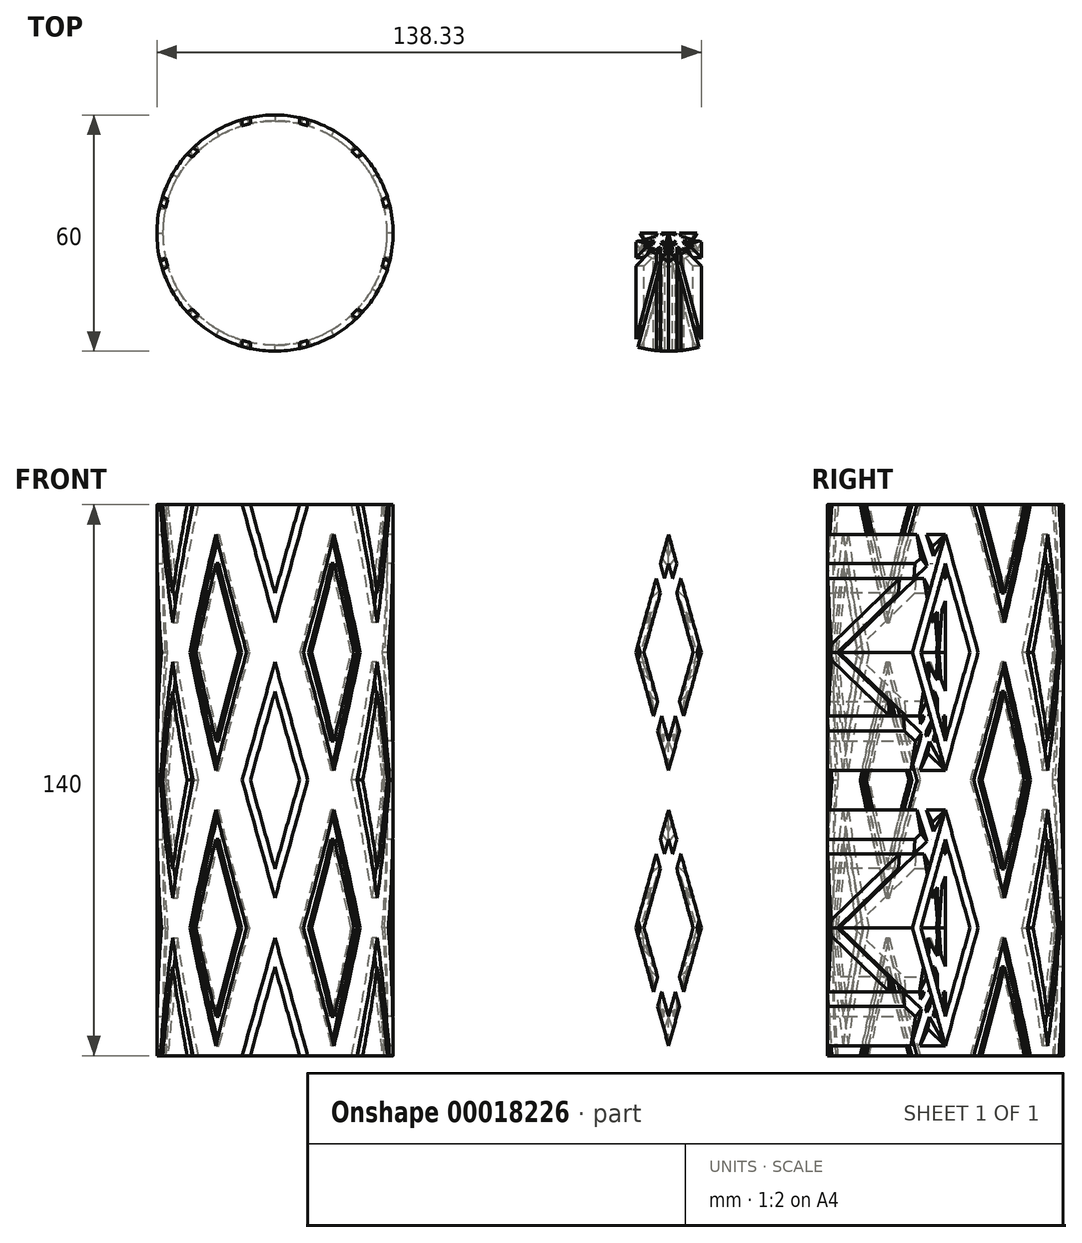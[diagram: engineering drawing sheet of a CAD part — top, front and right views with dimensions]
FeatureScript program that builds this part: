
annotation { "Feature Type Name" : "Feature", "Feature Type Description" : "" }
export const myFeature = defineFeature(function(context is Context, id is Id, definition is map)
    precondition{}
    {
        {
            var Q0;
            Q0=qCreatedBy(makeId("Top.planeOp"),FACE);
            var sketch = newSketch(context, id + "F0", { "sketchPlane" : qUnion([Q0])});
            skCircle(sketch, "E0", {"center": v(0, 0) * mm, "radius": 30 * mm});
            skCircle(sketch, "E1", {"center": v(0, 0) * mm, "radius": 28.5 * mm});
            skSolve(sketch);
        }
        {
            var Q0;
            Q0=makeQuery(id+"F0.imprint","IMPRINT",FACE,{"disambiguationData":[TD([[makeQuery(id+"F0.imprint","IMPRINT",EDGE,{"derivedFrom":sQuery(id+"F0.wireOp",EDGE,"E0")}),1.0]])]});
            extrude(context, id + "F1", {"entities" : qUnion([Q0]), "depth" : 140 * mm});
        }
        {
            var Q0;
            Q0=qCreatedBy(makeId("Front.planeOp"),FACE);
            var sketch = newSketch(context, id + "F2", { "sketchPlane" : qUnion([Q0])});
            skLineSegment(sketch, "E2", {"start": v(-6.25, 0) * mm, "end": v(0, 22.5) * mm});
            skLineSegment(sketch, "E3", {"start": v(0, 22.5) * mm, "end": v(6.25, 0) * mm});
            skLineSegment(sketch, "E4", {"start": v(-6.25, 0) * mm, "end": v(0, -22.5) * mm});
            skLineSegment(sketch, "E5", {"start": v(0, -22.5) * mm, "end": v(6.25, 0) * mm});
            skLineSegment(sketch, "E6", {"start": v(0, 47.5) * mm, "end": v(-6.25, 70) * mm});
            skLineSegment(sketch, "E7", {"start": v(-6.25, 70) * mm, "end": v(0, 92.5) * mm});
            skLineSegment(sketch, "E8", {"start": v(0, 92.5) * mm, "end": v(6.25, 70) * mm});
            skLineSegment(sketch, "E9", {"start": v(6.25, 70) * mm, "end": v(0, 47.5) * mm});
            skLineSegment(sketch, "E10", {"start": v(0, 117.5) * mm, "end": v(-6.25, 140) * mm});
            skLineSegment(sketch, "E11", {"start": v(-6.25, 140) * mm, "end": v(0, 162.5) * mm});
            skLineSegment(sketch, "E12", {"start": v(0, 162.5) * mm, "end": v(6.25, 140) * mm});
            skLineSegment(sketch, "E13", {"start": v(6.25, 140) * mm, "end": v(0, 117.5) * mm});
            skLineSegment(sketch, "E14", {"start": v(0, 140) * mm, "end": v(0, 0) * mm, "construction": true});
            skPoint(sketch, "E15", {"position": v(0, 70) * mm});
            skLineSegment(sketch, "E16", {"start": v(-6.25, 70) * mm, "end": v(6.25, 70) * mm, "construction": true});
            skLineSegment(sketch, "E17.0", {"start": v(-8.33, 140) * mm, "end": v(0, 169.97) * mm});
            skLineSegment(sketch, "E17.1", {"start": v(0, 110.03) * mm, "end": v(-8.33, 140) * mm});
            skLineSegment(sketch, "E17.2", {"start": v(8.33, 140) * mm, "end": v(0, 110.03) * mm});
            skLineSegment(sketch, "E17.3", {"start": v(0, 169.97) * mm, "end": v(8.33, 140) * mm});
            skLineSegment(sketch, "E18.0", {"start": v(0, 99.97) * mm, "end": v(8.33, 70) * mm});
            skLineSegment(sketch, "E18.1", {"start": v(-8.33, 70) * mm, "end": v(0, 99.97) * mm});
            skLineSegment(sketch, "E18.2", {"start": v(0, 40.03) * mm, "end": v(-8.33, 70) * mm});
            skLineSegment(sketch, "E18.3", {"start": v(8.33, 70) * mm, "end": v(0, 40.03) * mm});
            skLineSegment(sketch, "E19.0", {"start": v(0, 29.97) * mm, "end": v(8.33, 0) * mm});
            skLineSegment(sketch, "E19.1", {"start": v(-8.33, 0) * mm, "end": v(0, 29.97) * mm});
            skLineSegment(sketch, "E19.2", {"start": v(-8.33, 0) * mm, "end": v(0, -29.97) * mm});
            skLineSegment(sketch, "E19.3", {"start": v(0, -29.97) * mm, "end": v(8.33, 0) * mm});
            skSolve(sketch);
        }
        {
            var Q0;
            Q0=makeQuery(id+"F2.imprint","IMPRINT",FACE,{"disambiguationData":[TD([[makeQuery(id+"F2.imprint","IMPRINT",EDGE,{"derivedFrom":sQuery(id+"F2.wireOp",EDGE,"E10")}),1.0]])]});
            var Q1;
            Q1=makeQuery(id+"F2.imprint","IMPRINT",FACE,{"disambiguationData":[TD([[makeQuery(id+"F2.imprint","IMPRINT",EDGE,{"derivedFrom":sQuery(id+"F2.wireOp",EDGE,"E6")}),1.0]])]});
            var Q2;
            Q2=makeQuery(id+"F2.imprint","IMPRINT",FACE,{"disambiguationData":[TD([[makeQuery(id+"F2.imprint","IMPRINT",EDGE,{"derivedFrom":sQuery(id+"F2.wireOp",EDGE,"E2")}),1.0]])]});
            var Q3;
            Q3=makeQuery(id+"F1.opExtrude","SWEPT_FACE",FACE,{"disambiguationData":[OSD([sQuery(id+"F0.wireOp",EDGE,"E0")])]});
            extrude(context, id + "F3", {"entities" : qUnion([Q0, Q1, Q2]), "endBound" : BoundingType.UP_TO_SURFACE, "endBoundEntityFace" : qUnion([Q3]), "depth" : 25 * mm});
        }
        {
            var Q0;
            Q0=makeQuery(id+"F3.opExtrude","SWEPT_BODY",BODY,{"disambiguationData":[OSD([sQuery(id+"F2.wireOp",EDGE,"E6"),sQuery(id+"F2.wireOp",EDGE,"E7"),sQuery(id+"F2.wireOp",EDGE,"E8"),sQuery(id+"F2.wireOp",EDGE,"E9"),sQuery(id+"F2.wireOp",EDGE,"E18.0"),sQuery(id+"F2.wireOp",EDGE,"E18.1"),sQuery(id+"F2.wireOp",EDGE,"E18.2"),sQuery(id+"F2.wireOp",EDGE,"E18.3")])]});
            var Q1;
            Q1=makeQuery(id+"F3.opExtrude","SWEPT_BODY",BODY,{"disambiguationData":[OSD([sQuery(id+"F2.wireOp",EDGE,"E2"),sQuery(id+"F2.wireOp",EDGE,"E3"),sQuery(id+"F2.wireOp",EDGE,"E4"),sQuery(id+"F2.wireOp",EDGE,"E5"),sQuery(id+"F2.wireOp",EDGE,"E19.0"),sQuery(id+"F2.wireOp",EDGE,"E19.1"),sQuery(id+"F2.wireOp",EDGE,"E19.2"),sQuery(id+"F2.wireOp",EDGE,"E19.3")])]});
            var Q2;
            Q2=sQuery(id+"F2.wireOp",EDGE,"E14");
            transform(context, id + "F4", {"entities" : qUnion([Q0, Q1]), "transformType" : TransformType.TRANSLATION_DISTANCE, "transformDirection" : qUnion([Q2]), "distance" : 32.5 * mm, "oppositeDirection" : true, "makeCopy" : true});
        }
        {
            var Q0;
            Q0=makeQuery(id+"F4.opPattern","COPY",BODY,{"derivedFrom":makeQuery(id+"F3.opExtrude","SWEPT_BODY",BODY,{"disambiguationData":[OSD([sQuery(id+"F2.wireOp",EDGE,"E6"),sQuery(id+"F2.wireOp",EDGE,"E7"),sQuery(id+"F2.wireOp",EDGE,"E8"),sQuery(id+"F2.wireOp",EDGE,"E9"),sQuery(id+"F2.wireOp",EDGE,"E18.0"),sQuery(id+"F2.wireOp",EDGE,"E18.1"),sQuery(id+"F2.wireOp",EDGE,"E18.2"),sQuery(id+"F2.wireOp",EDGE,"E18.3")])]}),"instanceName":"1"});
            var Q1;
            Q1=makeQuery(id+"F4.opPattern","COPY",BODY,{"derivedFrom":makeQuery(id+"F3.opExtrude","SWEPT_BODY",BODY,{"disambiguationData":[OSD([sQuery(id+"F2.wireOp",EDGE,"E2"),sQuery(id+"F2.wireOp",EDGE,"E3"),sQuery(id+"F2.wireOp",EDGE,"E4"),sQuery(id+"F2.wireOp",EDGE,"E5"),sQuery(id+"F2.wireOp",EDGE,"E19.0"),sQuery(id+"F2.wireOp",EDGE,"E19.1"),sQuery(id+"F2.wireOp",EDGE,"E19.2"),sQuery(id+"F2.wireOp",EDGE,"E19.3")])]}),"instanceName":"1"});
            var Q2;
            {var subQ0=sQuery(id+"F0.wireOp",EDGE,"E0");Q2=makeQuery(id+"F7.boolean.opBoolean","SPLIT",EDGE,{"disambiguationData":[TD([makeQuery(id+"F3.opExtrude","SWEPT_FACE",FACE,{"disambiguationData":[OSD([sQuery(id+"F2.wireOp",EDGE,"E17.2")])]})])],"derivedFrom":makeQuery(id+"F1.opExtrude","CAP_EDGE",EDGE,{"disambiguationData":[OSD([subQ0])],"isStart":false})});}
            circularPattern(context, id + "F5", {"entities" : qUnion([Q0, Q1]), "axis" : qUnion([Q2]), "angle" : 30 * degree, "instanceCount" : 2});
        }
        {
            var Q0;
            Q0=makeQuery(id+"F5.opPattern","COPY",BODY,{"derivedFrom":makeQuery(id+"F4.opPattern","COPY",BODY,{"derivedFrom":makeQuery(id+"F3.opExtrude","SWEPT_BODY",BODY,{"disambiguationData":[OSD([sQuery(id+"F2.wireOp",EDGE,"E6"),sQuery(id+"F2.wireOp",EDGE,"E7"),sQuery(id+"F2.wireOp",EDGE,"E8"),sQuery(id+"F2.wireOp",EDGE,"E9"),sQuery(id+"F2.wireOp",EDGE,"E18.0"),sQuery(id+"F2.wireOp",EDGE,"E18.1"),sQuery(id+"F2.wireOp",EDGE,"E18.2"),sQuery(id+"F2.wireOp",EDGE,"E18.3")])]}),"instanceName":"1"}),"instanceName":"1"});
            var Q1;
            Q1=makeQuery(id+"F5.opPattern","COPY",BODY,{"derivedFrom":makeQuery(id+"F4.opPattern","COPY",BODY,{"derivedFrom":makeQuery(id+"F3.opExtrude","SWEPT_BODY",BODY,{"disambiguationData":[OSD([sQuery(id+"F2.wireOp",EDGE,"E2"),sQuery(id+"F2.wireOp",EDGE,"E3"),sQuery(id+"F2.wireOp",EDGE,"E4"),sQuery(id+"F2.wireOp",EDGE,"E5"),sQuery(id+"F2.wireOp",EDGE,"E19.0"),sQuery(id+"F2.wireOp",EDGE,"E19.1"),sQuery(id+"F2.wireOp",EDGE,"E19.2"),sQuery(id+"F2.wireOp",EDGE,"E19.3")])]}),"instanceName":"1"}),"instanceName":"1"});
            var Q2;
            Q2=makeQuery(id+"F1.opExtrude","CAP_EDGE",EDGE,{"disambiguationData":[OSD([sQuery(id+"F0.wireOp",EDGE,"E0")])],"isStart":false});
            circularPattern(context, id + "F6", {"operationType" : NewBodyOperationType.REMOVE, "entities" : qUnion([Q0, Q1]), "axis" : qUnion([Q2]), "angle" : 360 * degree, "instanceCount" : 6, "equalSpace" : true});
        }
        {
            var Q0;
            Q0=makeQuery(id+"F3.opExtrude","SWEPT_BODY",BODY,{"disambiguationData":[OSD([sQuery(id+"F2.wireOp",EDGE,"E10"),sQuery(id+"F2.wireOp",EDGE,"E11"),sQuery(id+"F2.wireOp",EDGE,"E12"),sQuery(id+"F2.wireOp",EDGE,"E13"),sQuery(id+"F2.wireOp",EDGE,"E17.0"),sQuery(id+"F2.wireOp",EDGE,"E17.1"),sQuery(id+"F2.wireOp",EDGE,"E17.2"),sQuery(id+"F2.wireOp",EDGE,"E17.3")])]});
            var Q1;
            Q1=makeQuery(id+"F3.opExtrude","SWEPT_BODY",BODY,{"disambiguationData":[OSD([sQuery(id+"F2.wireOp",EDGE,"E2"),sQuery(id+"F2.wireOp",EDGE,"E3"),sQuery(id+"F2.wireOp",EDGE,"E4"),sQuery(id+"F2.wireOp",EDGE,"E5"),sQuery(id+"F2.wireOp",EDGE,"E19.0"),sQuery(id+"F2.wireOp",EDGE,"E19.1"),sQuery(id+"F2.wireOp",EDGE,"E19.2"),sQuery(id+"F2.wireOp",EDGE,"E19.3")])]});
            var Q2;
            Q2=makeQuery(id+"F3.opExtrude","SWEPT_BODY",BODY,{"disambiguationData":[OSD([sQuery(id+"F2.wireOp",EDGE,"E6"),sQuery(id+"F2.wireOp",EDGE,"E7"),sQuery(id+"F2.wireOp",EDGE,"E8"),sQuery(id+"F2.wireOp",EDGE,"E9"),sQuery(id+"F2.wireOp",EDGE,"E18.0"),sQuery(id+"F2.wireOp",EDGE,"E18.1"),sQuery(id+"F2.wireOp",EDGE,"E18.2"),sQuery(id+"F2.wireOp",EDGE,"E18.3")])]});
            var Q3;
            Q3=makeQuery(id+"F1.opExtrude","CAP_EDGE",EDGE,{"disambiguationData":[OSD([sQuery(id+"F0.wireOp",EDGE,"E0")])],"isStart":false});
            circularPattern(context, id + "F7", {"operationType" : NewBodyOperationType.REMOVE, "entities" : qUnion([Q0, Q1, Q2]), "axis" : qUnion([Q3]), "angle" : 360 * degree, "instanceCount" : 6, "equalSpace" : true});
        }
        {
            var Q0;
            Q0=makeQuery(id+"F4.opPattern","COPY",BODY,{"derivedFrom":makeQuery(id+"F3.opExtrude","SWEPT_BODY",BODY,{"disambiguationData":[OSD([sQuery(id+"F2.wireOp",EDGE,"E2"),sQuery(id+"F2.wireOp",EDGE,"E3"),sQuery(id+"F2.wireOp",EDGE,"E4"),sQuery(id+"F2.wireOp",EDGE,"E5"),sQuery(id+"F2.wireOp",EDGE,"E19.0"),sQuery(id+"F2.wireOp",EDGE,"E19.1"),sQuery(id+"F2.wireOp",EDGE,"E19.2"),sQuery(id+"F2.wireOp",EDGE,"E19.3")])]}),"instanceName":"1"});
            var Q1;
            Q1=makeQuery(id+"F4.opPattern","COPY",BODY,{"derivedFrom":makeQuery(id+"F3.opExtrude","SWEPT_BODY",BODY,{"disambiguationData":[OSD([sQuery(id+"F2.wireOp",EDGE,"E6"),sQuery(id+"F2.wireOp",EDGE,"E7"),sQuery(id+"F2.wireOp",EDGE,"E8"),sQuery(id+"F2.wireOp",EDGE,"E9"),sQuery(id+"F2.wireOp",EDGE,"E18.0"),sQuery(id+"F2.wireOp",EDGE,"E18.1"),sQuery(id+"F2.wireOp",EDGE,"E18.2"),sQuery(id+"F2.wireOp",EDGE,"E18.3")])]}),"instanceName":"1"});
            transform(context, id + "F8", {"entities" : qUnion([Q0, Q1]), "transformType" : TransformType.TRANSLATION_3D, "dx" : 100 * mm, "dy" : 0 * mm, "dz" : 0 * mm, "makeCopy" : false});
        }
        {
            var Q0;
            Q0=qCreatedBy(makeId("Top.planeOp"),FACE);
            var sketch = newSketch(context, id + "F9", { "sketchPlane" : qUnion([Q0])});
            skCircle(sketch, "E20", {"center": v(0, 0) * mm, "radius": 28.5 * mm});
            skSolve(sketch);
        }
        {
            var Q0;
            Q0=makeQuery(id+"F9.imprint","IMPRINT",FACE,{"disambiguationData":[TD([[makeQuery(id+"F9.imprint","IMPRINT",EDGE,{"derivedFrom":sQuery(id+"F9.wireOp",EDGE,"E20")}),1.0]])]});
            extrude(context, id + "F10", {"entities" : qUnion([Q0]), "operationType" : NewBodyOperationType.ADD, "depth" : 140 * mm});
        }
    });
